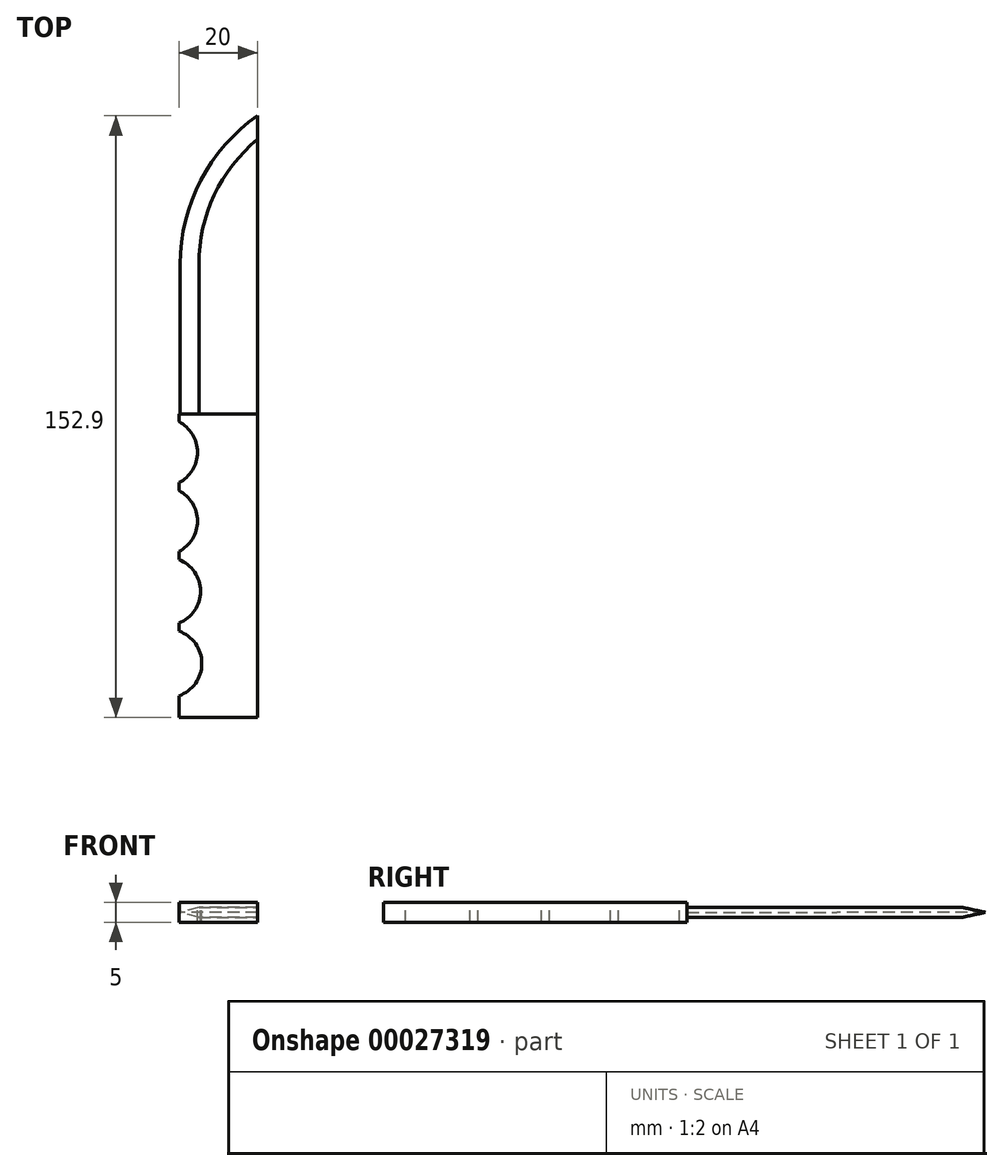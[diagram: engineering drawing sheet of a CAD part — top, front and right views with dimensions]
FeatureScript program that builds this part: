
annotation { "Feature Type Name" : "Feature", "Feature Type Description" : "" }
export const myFeature = defineFeature(function(context is Context, id is Id, definition is map)
    precondition{}
    {
        {
            var Q0;
            Q0=qCreatedBy(makeId("Top.planeOp"),FACE);
            var sketch = newSketch(context, id + "F0", { "sketchPlane" : qUnion([Q0])});
            skLineSegment(sketch, "E0.bottom", {"start": v(-45.98, 18.1) * mm, "end": v(-25.98, 18.1) * mm});
            skLineSegment(sketch, "E0.top", {"start": v(-45.98, -20) * mm, "end": v(-25.98, -20) * mm});
            skLineSegment(sketch, "E0.left", {"start": v(-45.98, 18.1) * mm, "end": v(-45.98, -20) * mm});
            skLineSegment(sketch, "E0.right", {"start": v(-25.98, 18.1) * mm, "end": v(-25.98, -20) * mm});
            skLineSegment(sketch, "E1", {"start": v(-25.98, 18.1) * mm, "end": v(-25.98, 56.2) * mm});
            skArc(sketch, "E2", {"start": v(-25.98, 56.2) * mm, "mid": v(-40.67, 39.6) * mm, "end": v(-45.98, 18.1) * mm});
            skLineSegment(sketch, "E3.bottom", {"start": v(-45.98, -20) * mm, "end": v(-25.99, -20) * mm});
            skSolve(sketch);
        }
        {
            var Q0;
            Q0 = qSketchRegion(id + "F0", true);
            extrude(context, id + "F1", {"entities" : qUnion([Q0]), "oppositeDirection" : true, "depth" : 1.27 * mm});
        }
        {
            var Q0;
            Q0 = qSketchRegion(id + "F0", true);
            extrude(context, id + "F2", {"entities" : qUnion([Q0]), "operationType" : NewBodyOperationType.ADD, "depth" : 1.27 * mm});
        }
        {
            var Q0;
            Q0=makeQuery(id+"F2.opExtrude","CAP_EDGE",EDGE,{"disambiguationData":[OSD([sQuery(id+"F0.wireOp",EDGE,"E2")])],"isStart":false});
            var Q1;
            Q1=makeQuery(id+"F2.opExtrude","CAP_EDGE",EDGE,{"disambiguationData":[OSD([sQuery(id+"F0.wireOp",EDGE,"E0.left")])],"isStart":false});
            chamfer(context, id + "F3", {"entities" : qUnion([Q0, Q1]), "chamferType" : ChamferType.OFFSET_ANGLE, "width" : 5.08 * mm, "oppositeDirection" : false, "angle" : 15 * degree});
        }
        {
            var Q0;
            Q0=makeQuery(id+"F1.opExtrude","CAP_EDGE",EDGE,{"disambiguationData":[OSD([sQuery(id+"F0.wireOp",EDGE,"E0.left")])],"isStart":false});
            var Q1;
            Q1=makeQuery(id+"F1.opExtrude","CAP_EDGE",EDGE,{"disambiguationData":[OSD([sQuery(id+"F0.wireOp",EDGE,"E2")])],"isStart":false});
            chamfer(context, id + "F4", {"entities" : qUnion([Q0, Q1]), "chamferType" : ChamferType.OFFSET_ANGLE, "width" : 5.08 * mm, "oppositeDirection" : true, "angle" : 15 * degree});
        }
        {
            var Q0;
            Q0=qCreatedBy(makeId("Top.planeOp"),FACE);
            var sketch = newSketch(context, id + "F5", { "sketchPlane" : qUnion([Q0])});
            skLineSegment(sketch, "E4", {"start": v(-45.98, -19.97) * mm, "end": v(-45.98, -21.97) * mm});
            skLineSegment(sketch, "E5.top", {"start": v(-45.98, -19.97) * mm, "end": v(-25.98, -19.97) * mm});
            skArc(sketch, "E6", {"start": v(-45.98, -37.47) * mm, "mid": v(-41.25, -29.72) * mm, "end": v(-45.98, -21.97) * mm});
            skLineSegment(sketch, "E7", {"start": v(-25.98, -19.97) * mm, "end": v(-26, -97.12) * mm});
            skLineSegment(sketch, "E8", {"start": v(-45.98, -37.47) * mm, "end": v(-45.98, -39.47) * mm});
            skLineSegment(sketch, "E9", {"start": v(-45.98, -54.97) * mm, "end": v(-45.98, -56.97) * mm});
            skLineSegment(sketch, "E10", {"start": v(-45.98, -73.15) * mm, "end": v(-45.98, -75.15) * mm});
            skArc(sketch, "E11", {"start": v(-45.98, -73.15) * mm, "mid": v(-40.5, -65.06) * mm, "end": v(-45.98, -56.97) * mm});
            skArc(sketch, "E12", {"start": v(-45.98, -91.6) * mm, "mid": v(-40.15, -83.37) * mm, "end": v(-45.98, -75.15) * mm});
            skLineSegment(sketch, "E13.top", {"start": v(-45.98, -97.12) * mm, "end": v(-26, -97.12) * mm});
            skLineSegment(sketch, "E14", {"start": v(-45.98, -91.6) * mm, "end": v(-45.98, -97.12) * mm});
            skArc(sketch, "E15", {"start": v(-45.98, -54.97) * mm, "mid": v(-41.24, -47.22) * mm, "end": v(-45.98, -39.47) * mm});
            skSolve(sketch);
        }
        {
            var Q0;
            Q0 = qSketchRegion(id + "F5", true);
            extrude(context, id + "F6", {"entities" : qUnion([Q0]), "operationType" : NewBodyOperationType.ADD, "oppositeDirection" : true, "depth" : 2.5 * mm});
        }
        {
            var Q0;
            Q0=makeQuery(id+"F6.opExtrude","CAP_FACE",FACE,{"disambiguationData":[OSD([sQuery(id+"F5.wireOp",EDGE,"E4"),sQuery(id+"F5.wireOp",EDGE,"E5.top"),sQuery(id+"F5.wireOp",EDGE,"E6"),sQuery(id+"F5.wireOp",EDGE,"E7"),sQuery(id+"F5.wireOp",EDGE,"E8"),sQuery(id+"F5.wireOp",EDGE,"E9"),sQuery(id+"F5.wireOp",EDGE,"E10"),sQuery(id+"F5.wireOp",EDGE,"E11"),sQuery(id+"F5.wireOp",EDGE,"E12"),sQuery(id+"F5.wireOp",EDGE,"E13.top"),sQuery(id+"F5.wireOp",EDGE,"E14"),sQuery(id+"F5.wireOp",EDGE,"E15")])],"isStart":true});
            extrude(context, id + "F7", {"entities" : qUnion([Q0]), "operationType" : NewBodyOperationType.ADD, "depth" : 2.5 * mm});
        }
    });
